# Revit family: Maxlogic Оповещатели световые, звуковые, светозвуковые (Высокий класс защиты IP)
name_source: partatom
category: Fire Alarm Devices
units: mm (PartAtom-declared; Revit-internal decimal feet)

## family parameters
Cut with Voids When Loaded = No
Host = Face
Maintain Annotation Orientation = Yes
OmniClass Number = 23.85.30.21
OmniClass Title = Environmental Detection/Registration
Part Type = Normal
Room Calculation Point = No
Round Connector Dimension = Use Diameter
Shared = No

## types (18) — shared parameters
Manufacturer = Mavili Elektronik Ticaret A.Ş.
Model = Maxlogic
URL = https://www.mavili.com.tr
Адрес №1 = Şerifali Mahallesi Kutup Sokak No:27/1-2-4 Ümraniye TR-34775 İSTANBUL
Вторичный материал = Пластмассовый
Гарантийный срок = Года
Гарантийный срок запчастей = 2
Гарантия срока службы = 2
Главный Материал = Красный пластмассовый PC/ABS
Инструкция по установке = https://mavilielektronik.com
Монтажная высота = Выше пола на 240 см
Монтажная поверхность = Настенная
Номер телефона = (+)90 216 466 45 05
Номер факса = (+)90 216 466 45 10
Номинальная высота = 95 мм
Номинальная ширина = 95 мм
Рабочая Температура = (-25°C) - (+70°C)
Рабочее напряжение (по умолчанию) = 24 В Пост. ток
Цвет = Красный
zero-valued in all types: Cost, Default Elevation

## per-type parameters (varying)
| type | Description | IP 33 нижняя часть | IP 65 верхняя часть | Верхняя часть звукового оповещателя | Верхняя часть звукового, светозвукогого, светового оповещателя | Вес | Диапазон рабочего напряжения | Класс защиты | Код продукта | Настройка адреса устройства | Номинальная глубина | Производительность кода | Световой оповещатель |
| Maxlogic Неадресный оповещатель, погодоустойчивый (IP33) | Неадресный оповещатель, погодоустойчивый (IP33) | Yes | No | Yes | No | 154 гр | 21-28В Пост. ток | IP 33 | ML-2440 |  | 82 мм | EN 54-3 | No |
| Maxlogic Неадресный световой оповещатель,погодоустойчивый (IP33) | Неадресный световой оповещатель,погодоустойчивый (IP33) | Yes | No | No | Yes | 149 гр | 21-28В Пост. ток | IP 33 | ML-2450 |  | 82 мм | EN 54-23 | Yes |
| Maxlogic Неадресный светозвуковой оповещатель, погодоустойчивый (IP33) | Неадресный светозвуковой оповещатель, погодоустойчивый (IP33) | Yes | No | No | Yes | 166 гр | 21-28В Пост. ток | IP 33 | ML-2460 |  | 82 мм | EN 54-3 / EN 54-23 | Yes |
| Maxlogic Неадресный оповещатель, погодоустойчивый (IP65) | Неадресный оповещатель, погодоустойчивый (IP65) | No | Yes | Yes | No | 173 гр | 21-28В Пост. ток | IP 65 | ML-2470 |  | 100 мм | EN 54-3 | No |
| Maxlogic Неадресный световой оповещатель, погодоустойчивый (IP65) | Неадресный световой оповещатель, погодоустойчивый (IP65) | No | Yes | No | Yes | 168 гр | 21-28В Пост. ток | IP 65 | ML-2480 |  | 107 мм | EN 54-23 | Yes |
| Maxlogic Неадресный светозвуковой оповещатель, погодоустойчивый (IP65) | Неадресный светозвуковой оповещатель, погодоустойчивый (IP65) | No | Yes | No | Yes | 185 гр | 21-28В Пост. ток | IP 65 | ML-2490 |  | 107 мм | EN 54-3 / EN 54-23 | Yes |
| Maxlogic Адресный оповещатель, погодоустойчивый (IP33) | Адресный оповещатель, погодоустойчивый (IP33) | Yes | No | Yes | No | 159 гр | 18-33В Пост. ток | IP 33 | ML-1440 | Модульная адресация | 82 мм | EN 54-3 | No |
| Maxlogic Адресный оповещатель, погодоустойчивый (IP33), с изолятором КЗ | Адресный оповещатель, погодоустойчивый (IP33), с изолятором КЗ | Yes | No | Yes | No | 159 гр | 18-33В Пост. ток | IP 33 | ML-1440.SCI | Модульная адресация | 82 мм | EN 54-3 | No |
| MaxlogicАдресный световой оповещатель, погодоустойчивый (IP33) | Адресный световой оповещатель, погодоустойчивый (IP33) | Yes | No | No | Yes | 153 гр | 18-33В Пост. ток | IP 33 | ML-1450 | Модульная адресация | 82 мм | EN 54-23 | Yes |
| Maxlogic Адресный световой оповещатель, погодоустойчивый (IP33), с изолятором КЗ | Адресный световой оповещатель, погодоустойчивый (IP33), с изолятором КЗ | Yes | No | No | Yes | 153 гр | 18-33В Пост. ток | IP 33 | ML-1450.SCI | Модульная адресация | 82 мм | EN 54-23 | Yes |
| Maxlogic  Адресный светозвуковой оповещатель, погодоустойчивый (IP33) | Адресный светозвуковой оповещатель, погодоустойчивый (IP33) | Yes | No | No | Yes | 169 гр | 18-33В Пост. ток | IP 33 | ML-1460 | Модульная адресация | 82 мм | EN 54-3 / EN 54-23 | Yes |
| Maxlogic  Адресный светозвуковой оповещатель, погодоустойчивый (IP33), c изолятором КЗ | Адресный светозвуковой оповещатель, погодоустойчивый (IP33), c изолятором КЗ | Yes | No | No | Yes | 169 гр | 18-33В Пост. ток | IP 33 | ML-1460.SCI | Модульная адресация | 82 мм | EN 54-3 / EN 54-23 | Yes |
| Maxlogic Адресный оповещатель, погодоустойчивый (IP65) | Адресный оповещатель, погодоустойчивый (IP65) | No | Yes | Yes | No | 178 гр | 18-33В Пост. ток | IP 65 | ML-1470 | Модульная адресация | 82 мм | EN 54-3 | No |
| Maxlogic Адресный оповещатель, погодоустойчивый (IP65), с изолятором КЗ | Адресный оповещатель, погодоустойчивый (IP65), с изолятором КЗ | No | Yes | Yes | No | 178 гр | 18-33В Пост. ток | IP 65 | ML-1470.SCI | Модульная адресация | 82 мм | EN 54-3 | No |
| Maxlogic Адресный световой оповещатель, погодоустойчивый (IP65) | Адресный световой оповещатель, погодоустойчивый (IP65) | No | Yes | No | Yes | 172 гр | 18-33В Пост. ток | IP 65 | ML-1480 | Модульная адресация | 82 мм | EN 54-23 | Yes |
| Maxlogic Адресный световой оповещатель, погодоустойчивый (IP65), с изолятором КЗ | Адресный световой оповещатель, погодоустойчивый (IP65), с изолятором КЗ | No | Yes | No | Yes | 172 гр | 18-33В Пост. ток | IP 65 | ML-1480.SCI | Модульная адресация | 82 мм | EN 54-23 | Yes |
| Maxlogic Адресный светозвуковой оповещатель, погодоустойчивый (IP65) | Akıllı Adresli Sistem Flaşörlü siren | No | Yes | No | Yes | 188 гр | 18-33В Пост. ток | IP 65 | ML-1490 | Модульная адресация | 82 мм | EN 54-3 / EN 54-23 | Yes |
| Maxlogic Адресный светозвуковой оповещатель, погодоустойчивый (IP65), с изолятором КЗ | Адресный светозвуковой оповещатель, погодоустойчивый (IP65), с изолятором КЗ | No | Yes | No | Yes | 188 гр | 18-33В Пост. ток | IP 65 | ML-1490.SCI | Модульная адресация | 82 мм | EN 54-3 / EN 54-23 | Yes |

## geometry (parser evidence)
native form markers: Sweep x4
no freeform markers — native parametric forms only
